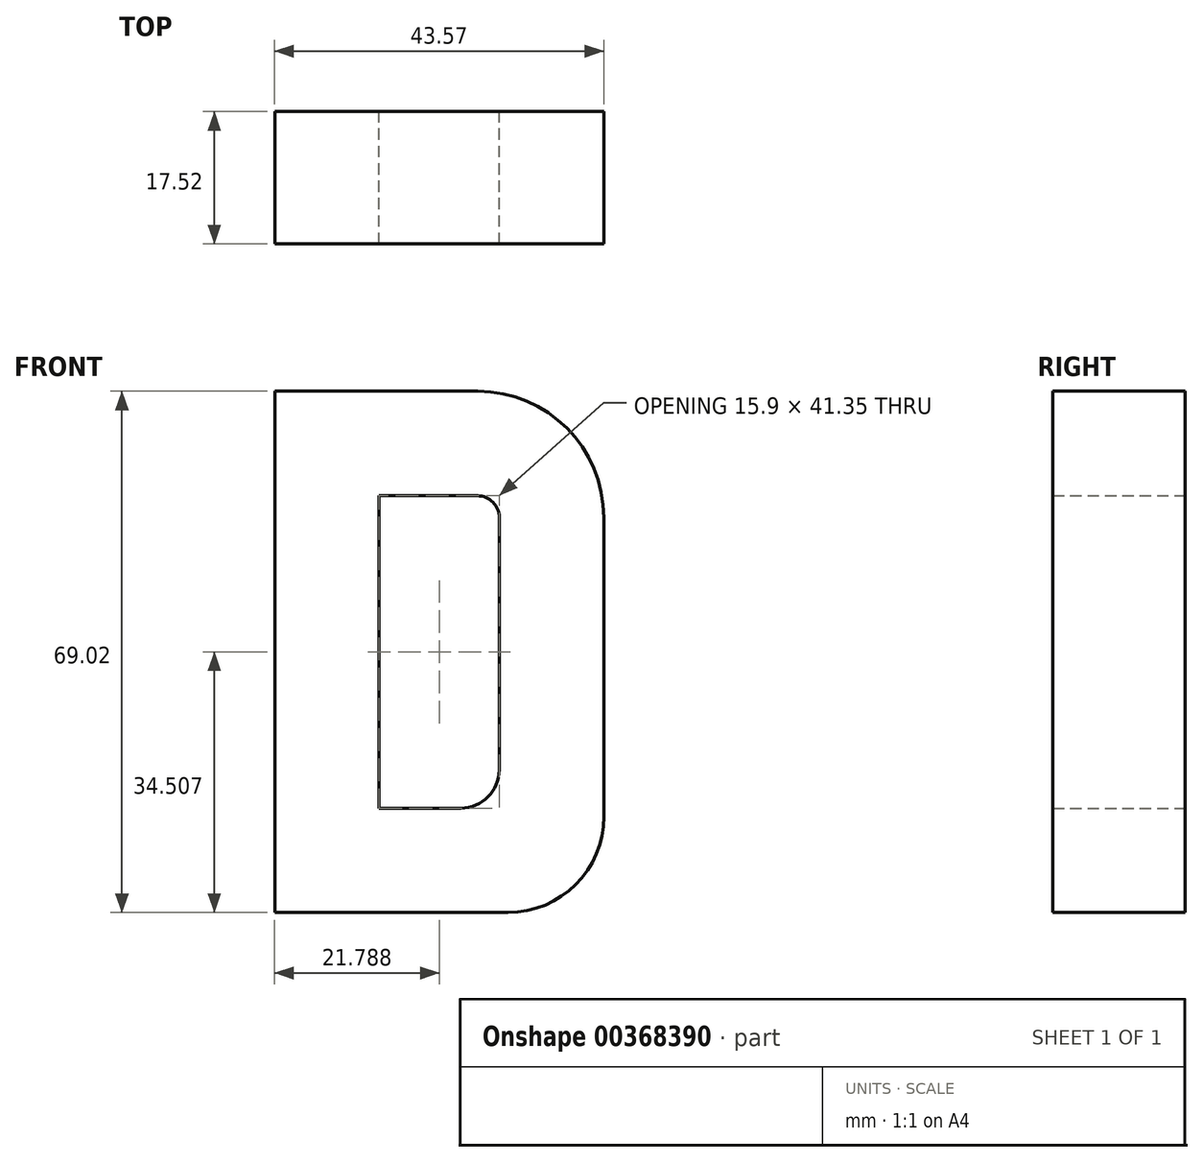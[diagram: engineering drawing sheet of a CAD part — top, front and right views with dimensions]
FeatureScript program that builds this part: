
annotation { "Feature Type Name" : "Feature", "Feature Type Description" : "" }
export const myFeature = defineFeature(function(context is Context, id is Id, definition is map)
    precondition{}
    {
        {
            var Q0;
            Q0=qCreatedBy(makeId("Front.planeOp"),FACE);
            var sketch = newSketch(context, id + "F0", { "sketchPlane" : qUnion([Q0])});
            skLineSegment(sketch, "E0", {"start": v(-71.46, 0) * mm, "end": v(-71.46, 55.61) * mm});
            skLineSegment(sketch, "E1", {"start": v(-71.46, 55.61) * mm, "end": v(-51.3, 55.61) * mm});
            skLineSegment(sketch, "E2", {"start": v(-41.3, 45.61) * mm, "end": v(-41.3, 0) * mm});
            skLineSegment(sketch, "E3", {"start": v(-41.3, 0) * mm, "end": v(-71.46, 0) * mm});
            skPoint(sketch, "E4.visualSharp", {"position": v(-41.3, 55.61) * mm});
            skArc(sketch, "E4.filletArc", {"start": v(-41.3, 45.61) * mm, "mid": v(-44.23, 52.68) * mm, "end": v(-51.3, 55.61) * mm});
            skSolve(sketch);
        }
        {
            var Q0;
            Q0=qCreatedBy(makeId("Top.planeOp"),FACE);
            var sketch = newSketch(context, id + "F1", { "sketchPlane" : qUnion([Q0])});
            skLineSegment(sketch, "E5.bottom", {"start": v(-34.6, -8.76) * mm, "end": v(-48.43, -8.76) * mm});
            skLineSegment(sketch, "E5.top", {"start": v(-34.6, 8.76) * mm, "end": v(-48.43, 8.76) * mm});
            skLineSegment(sketch, "E5.left", {"start": v(-34.6, -8.76) * mm, "end": v(-34.6, 8.76) * mm});
            skLineSegment(sketch, "E5.right", {"start": v(-48.43, -8.76) * mm, "end": v(-48.43, 8.76) * mm});
            skPoint(sketch, "E5.middle", {"position": v(-41.51, 0) * mm});
            skSolve(sketch);
        }
        {
            var Q0;
            Q0=makeQuery(id+"F1.imprint","IMPRINT",FACE,{"disambiguationData":[TD([[makeQuery(id+"F1.imprint","IMPRINT",EDGE,{"derivedFrom":sQuery(id+"F1.wireOp",EDGE,"E5.bottom")}),-1.0]])]});
            var Q1;
            Q1=sQuery(id+"F0.wireOp",EDGE,"E2");
            var Q2;
            Q2=sQuery(id+"F0.wireOp",EDGE,"E4.filletArc");
            var Q3;
            Q3=sQuery(id+"F0.wireOp",EDGE,"E1");
            var Q4;
            Q4=sQuery(id+"F0.wireOp",EDGE,"E0");
            var Q5;
            Q5=sQuery(id+"F0.wireOp",EDGE,"E3");
            sweep(context, id + "F2", {"profiles" : qUnion([Q0]), "path" : qUnion([Q1, Q2, Q3, Q4, Q5])});
        }
        {
            var Q0;
            Q0=makeQuery(id+"F2.opSweep","CAP_EDGE",EDGE,{"disambiguationData":[OSD([sQuery(id+"F0.wireOp",VERTEX,"E3.start"),sQuery(id+"F1.wireOp",EDGE,"E5.left")])],"isStart":true});
            fillet(context, id + "F3", {"entities" : qUnion([Q0]), "radius" : 12.7 * mm, "tangentPropagation" : true, "allowEdgeOverflow" : false});
        }
        {
            var Q0;
            Q0=makeQuery(id+"F2.opSweep","CAP_EDGE",EDGE,{"disambiguationData":[OSD([sQuery(id+"F0.wireOp",VERTEX,"E3.start"),sQuery(id+"F1.wireOp",EDGE,"E5.right")])],"isStart":true});
            fillet(context, id + "F4", {"entities" : qUnion([Q0]), "radius" : 5.08 * mm, "tangentPropagation" : true, "allowEdgeOverflow" : false});
        }
    });
